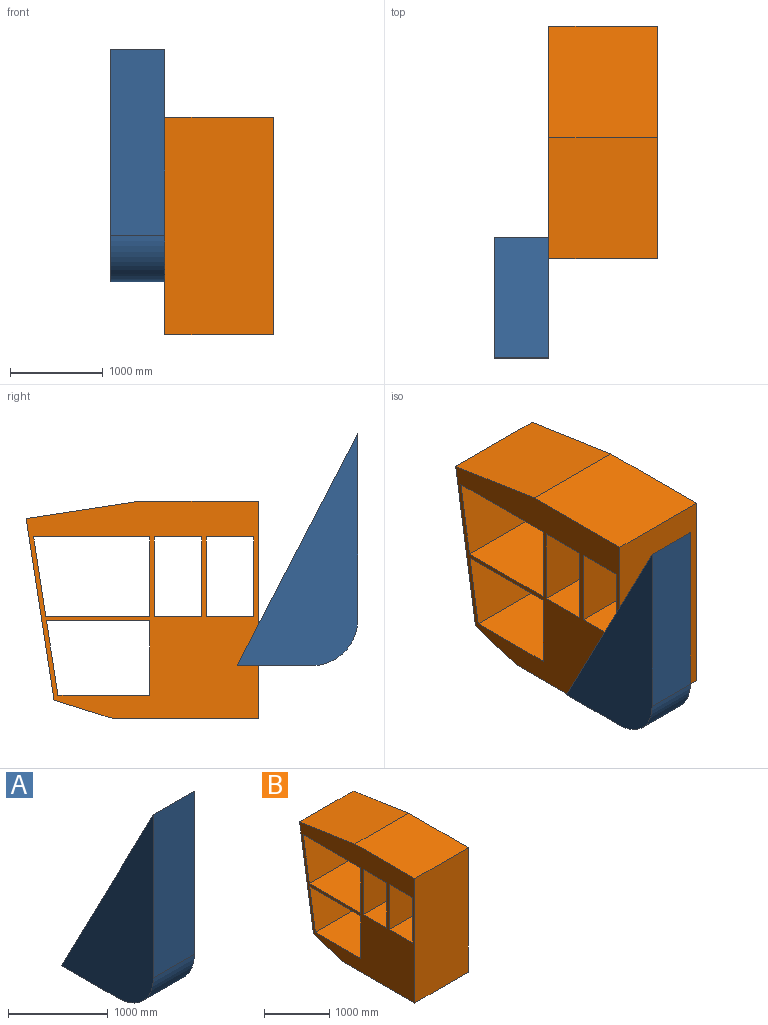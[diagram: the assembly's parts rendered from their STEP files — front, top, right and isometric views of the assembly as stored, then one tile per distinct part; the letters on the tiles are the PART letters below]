
ASSEMBLY  parts=2 mates=2
PART A: 6 faces, bbox 581x1300x2500 mm
  f0: plane 2000x581mm, normal (0,-1,0), area 1162000mm2, adj f2,f3,f4,f5
  f1: plane 800x581mm, normal (0,0,-1), area 464800mm2, adj f2,f3,f4,f5
  f2: plane 2500x1300mm, normal (0,0.89,0.46), area 1637142.1mm2, adj f0,f1,f3,f4
  f3: plane 2500x1300mm, normal (1,0,0), area 1571349.5mm2, adj f0,f1,f2,f5
  f4: plane 2500x1300mm, normal (-1,0,0), area 1571349.5mm2, adj f0,f1,f2,f5
  f5: cylinder r=500mm len=581mm, axis (-1,0,0), area 456316.3mm2, adj f0,f1,f3,f4
PART B: 24 faces, bbox 1162x2500x2336 mm
  f0: plane 2500x2336mm, normal (1,0,0), area 2594331.3mm2, adj f2,f3,f4,f5,f6,f7,f8,f9
  f1: plane 2500x2336mm, normal (-1,0,0), area 2594331.3mm2, adj f2,f3,f4,f5,f6,f7,f8,f9
  f2: plane 2336x1162mm, normal (0,-1,0), area 2714432mm2, adj f0,f1,f3,f7
  f3: plane 1564.89x1162mm, normal (0,0,-1), area 1818401.7mm2, adj f0,f1,f2,f4
  f4: plane 1162x635.09mm, normal (0,0.3,-0.95), area 773705mm2, adj f0,f1,f3,f5
  f5: plane 1951.52x1162mm, normal (0,0.99,-0.15), area 2294303.8mm2, adj f0,f1,f4,f6
  f6: plane 1200x1162mm, normal (0,0.15,0.99), area 1410781.9mm2, adj f0,f1,f5,f7
  f7: plane 1300x1162mm, normal (0,0,1), area 1510600mm2, adj f0,f1,f2,f6
  f8: plane 1162x988.06mm, normal (0,0,1), area 1148127.5mm2, adj f0,f1,f9,f11
  f9: plane 1162x801.84mm, normal (0,-0.99,0.15), area 942679.7mm2, adj f0,f1,f8,f10
  f10: plane 1162x1111.33mm, normal (0,0,-1), area 1291368.5mm2, adj f0,f1,f9,f11
  f11: plane 1162x801.84mm, normal (0,1,0), area 931733.3mm2, adj f0,f1,f8,f10
  f12: plane 1162x851.84mm, normal (0,-0.99,0.15), area 1001462.3mm2, adj f0,f1,f13,f15
  f13: plane 1249.98x1162mm, normal (0,0,-1), area 1452473.6mm2, adj f0,f1,f12,f14
  f14: plane 1162x851.84mm, normal (0,1,0), area 989833.3mm2, adj f0,f1,f13,f15
  f15: plane 1162x1119.02mm, normal (0,0,1), area 1300300.5mm2, adj f0,f1,f12,f14
  f16: plane 1162x509.51mm, normal (0,0,-1), area 592050.3mm2, adj f0,f1,f17,f19
  f17: plane 1162x851.84mm, normal (0,1,0), area 989833.3mm2, adj f0,f1,f16,f18
  f18: plane 1162x509.51mm, normal (0,0,1), area 592050.3mm2, adj f0,f1,f17,f19
  f19: plane 1162x851.84mm, normal (0,-1,0), area 989833.3mm2, adj f0,f1,f16,f18
  f20: plane 1162x851.84mm, normal (0,-1,0), area 989833.3mm2, adj f0,f1,f21,f23
  f21: plane 1162x509.51mm, normal (0,0,-1), area 592050.3mm2, adj f0,f1,f20,f22
  f22: plane 1162x851.84mm, normal (0,1,0), area 989833.3mm2, adj f0,f1,f21,f23
  f23: plane 1162x509.51mm, normal (0,0,1), area 592050.3mm2, adj f0,f1,f20,f22
PLACE A at identity fixed
PLACE B t=(581,3689,-2656.6)mm
MATE parallel B.f2 <-> A.f0  axis (0,-1,0) through (1162,1270,-1900)mm
MATE planar B.f1 <-> A.f3  axis (-1,0,0) through (581,2189.84,-1957.85)mm
